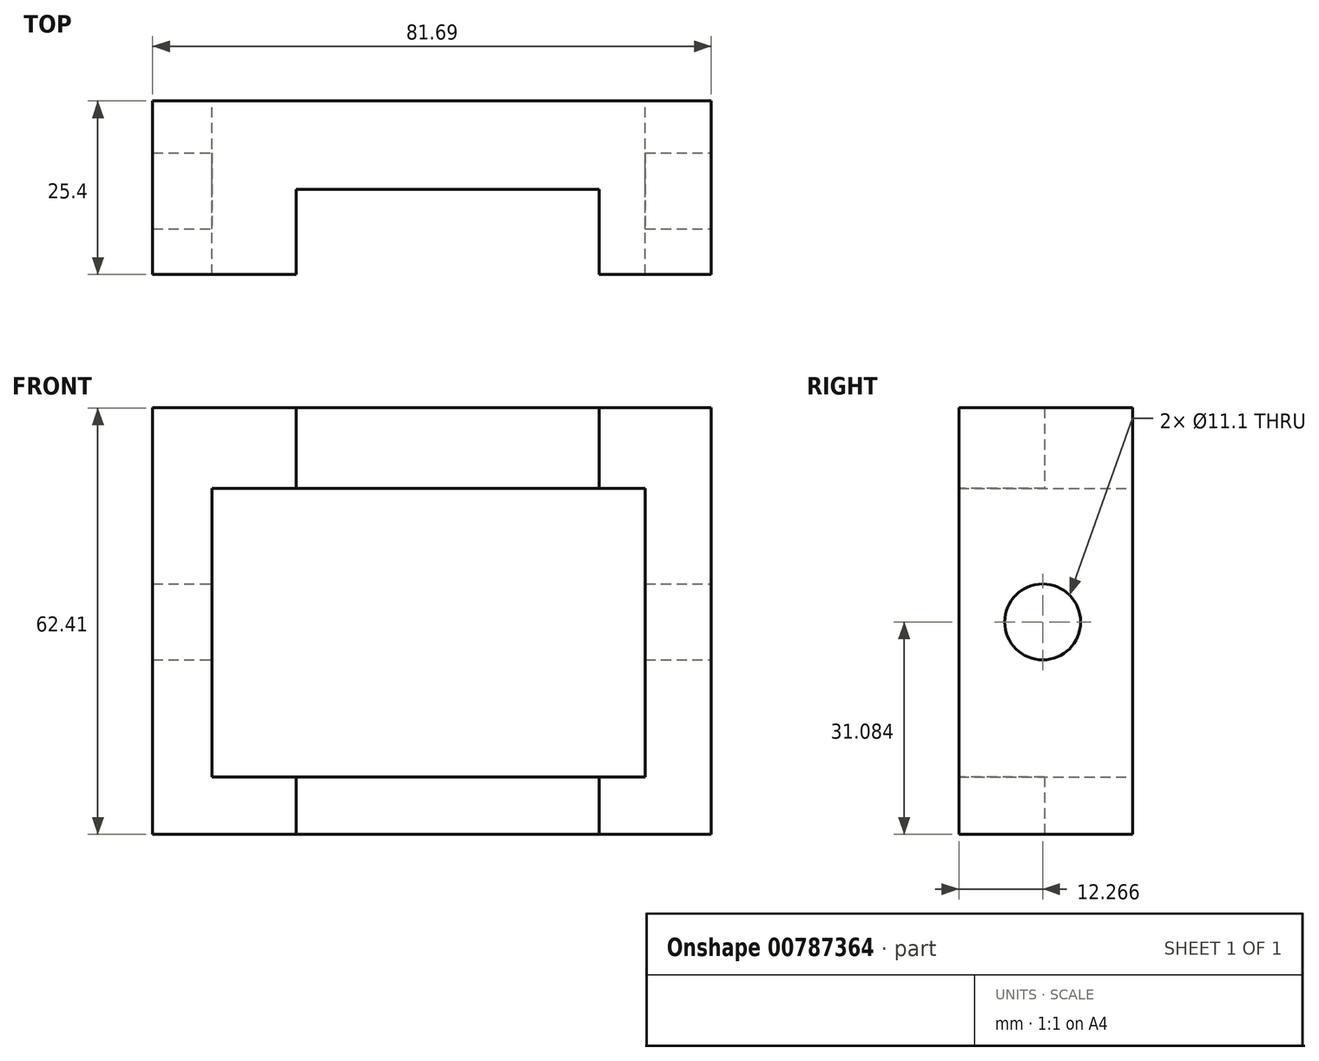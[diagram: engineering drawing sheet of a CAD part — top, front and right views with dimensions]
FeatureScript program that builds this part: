
annotation { "Feature Type Name" : "Feature", "Feature Type Description" : "" }
export const myFeature = defineFeature(function(context is Context, id is Id, definition is map)
    precondition{}
    {
        {
            var Q0;
            Q0=qCreatedBy(makeId("Front.planeOp"),FACE);
            var sketch = newSketch(context, id + "F0", { "sketchPlane" : qUnion([Q0])});
            skLineSegment(sketch, "E0.bottom", {"start": v(-36.03, -9.52) * mm, "end": v(27.35, -9.52) * mm});
            skLineSegment(sketch, "E0.top", {"start": v(-36.03, -17.95) * mm, "end": v(27.35, -17.95) * mm});
            skLineSegment(sketch, "E0.left", {"start": v(-36.03, -9.52) * mm, "end": v(-36.03, -17.95) * mm});
            skLineSegment(sketch, "E0.right", {"start": v(27.35, -9.52) * mm, "end": v(27.35, -17.95) * mm});
            skLineSegment(sketch, "E1.bottom", {"start": v(-36.03, -17.95) * mm, "end": v(-44.7, -17.95) * mm});
            skLineSegment(sketch, "E1.top", {"start": v(-36.03, 32.65) * mm, "end": v(-44.7, 32.65) * mm});
            skLineSegment(sketch, "E1.left", {"start": v(-36.03, -17.95) * mm, "end": v(-36.03, 32.65) * mm});
            skLineSegment(sketch, "E1.right", {"start": v(-44.7, -17.95) * mm, "end": v(-44.7, 32.65) * mm});
            skLineSegment(sketch, "E2.bottom", {"start": v(-44.7, 32.65) * mm, "end": v(27.35, 32.65) * mm});
            skLineSegment(sketch, "E2.top", {"start": v(-44.7, 44.46) * mm, "end": v(27.35, 44.46) * mm});
            skLineSegment(sketch, "E2.left", {"start": v(-44.7, 32.65) * mm, "end": v(-44.7, 44.46) * mm});
            skLineSegment(sketch, "E2.right", {"start": v(27.35, 32.65) * mm, "end": v(27.35, 44.46) * mm});
            skLineSegment(sketch, "E3.bottom", {"start": v(27.35, 44.46) * mm, "end": v(37, 44.46) * mm});
            skLineSegment(sketch, "E3.top", {"start": v(27.35, -17.95) * mm, "end": v(37, -17.95) * mm});
            skLineSegment(sketch, "E3.left", {"start": v(27.35, 44.46) * mm, "end": v(27.35, -17.95) * mm});
            skLineSegment(sketch, "E3.right", {"start": v(37, 44.46) * mm, "end": v(37, -17.95) * mm});
            skSolve(sketch);
        }
        {
            var Q0;
            Q0 = qSketchRegion(id + "F0", true);
            extrude(context, id + "F1", {"entities" : qUnion([Q0]), "depth" : 25.4 * mm, "offsetDistance" : 25.4 * mm});
        }
        {
            var Q0;
            Q0=makeQuery(id+"F1.opExtrude","SWEPT_FACE",FACE,{"disambiguationData":[OSD([sQuery(id+"F0.wireOp",EDGE,"E0.top"),sQuery(id+"F0.wireOp",EDGE,"E1.bottom"),sQuery(id+"F0.wireOp",EDGE,"E3.top")])]});
            var sketch = newSketch(context, id + "F2", { "sketchPlane" : qUnion([Q0])});
            skLineSegment(sketch, "E4.bottom", {"start": v(-23.74, 25.4) * mm, "end": v(20.6, 25.4) * mm});
            skLineSegment(sketch, "E4.top", {"start": v(-23.74, 12.9) * mm, "end": v(20.6, 12.9) * mm});
            skLineSegment(sketch, "E4.left", {"start": v(-23.74, 25.4) * mm, "end": v(-23.74, 12.9) * mm});
            skLineSegment(sketch, "E4.right", {"start": v(20.6, 25.4) * mm, "end": v(20.6, 12.9) * mm});
            skSolve(sketch);
        }
        {
            var Q0;
            Q0=makeQuery(id+"F2.imprint","IMPRINT",FACE,{"disambiguationData":[TD([[makeQuery(id+"F2.imprint","IMPRINT",EDGE,{"derivedFrom":sQuery(id+"F2.wireOp",EDGE,"E4.bottom")}),-1.0]])]});
            extrude(context, id + "F3", {"entities" : qUnion([Q0]), "operationType" : NewBodyOperationType.REMOVE, "oppositeDirection" : true, "depth" : 100.84 * mm, "offsetDistance" : 25.4 * mm});
        }
        {
            var Q0;
            Q0=makeQuery(id+"F1.opExtrude","SWEPT_FACE",FACE,{"disambiguationData":[OSD([sQuery(id+"F0.wireOp",EDGE,"E3.right")])]});
            var sketch = newSketch(context, id + "F4", { "sketchPlane" : qUnion([Q0])});
            skCircle(sketch, "E5", {"center": v(-13.13, 13.13) * mm, "radius": 5.55 * mm});
            skSolve(sketch);
        }
        {
            var Q0;
            Q0 = qSketchRegion(id + "F4", true);
            extrude(context, id + "F5", {"entities" : qUnion([Q0]), "operationType" : NewBodyOperationType.REMOVE, "oppositeDirection" : true, "depth" : 130.05 * mm, "offsetDistance" : 25.4 * mm});
        }
    });
